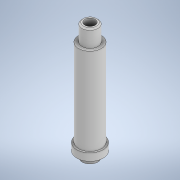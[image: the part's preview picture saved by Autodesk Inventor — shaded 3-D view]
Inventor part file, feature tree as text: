
AUTODESK INVENTOR PART (.ipt)
format: ipt  version: 2021 (Build 250183000, 183)  size: 130,560 bytes
history: native  units: mm
features: sketch x5, extrude x4, hole x1, chamfer x1
ambient origin geometry x8: Origin, YZ Plane, XZ Plane, XY Plane, X Axis, Y Axis, Z Axis, Center Point
bodies: Solid1 (feature_tree)
feature tree (11):
  extrude  "Extrusion1"  Depth=4.826mm TaperAngle=0.0deg
  extrude  "Extrusion2"  Depth=35.866mm TaperAngle=0.0deg
  extrude  "Extrusion3"  Depth=2.2mm
  hole  "Hole2"  [1 undecoded]
  extrude  "Extrusion4"  Depth=6.1mm TaperAngle=45.0deg
  chamfer  "Chamfer3"  [1 undecoded]
  sketch  "Sketch1"  dims[d0=9.398mm d1=4.826mm d2=0.0mm]
  sketch  "Sketch2"  dims[d3=8.15mm d4=35.866mm d5=0.0mm]
  sketch  "Sketch3"  dims[d6=2.2mm d7=0.0mm d18=5.5mm]
  sketch  "Sketch5"  dims[d19=3.7mm d20=6.0mm d21=4.0mm d22=2.0mm d23=90.0deg d24=8.0mm d25=20.594885mm d29=5.7mm]
  sketch  "Sketch6"  dims[d30=6.1mm d31=0.0mm d32=0.5mm d33=2.0mm d34=45.0deg]
note: 2 required parameter values undecoded (feature->parameter linkage not recoverable at this tier; creation-order binding heuristic only, values carry confidence <= 0.55)
